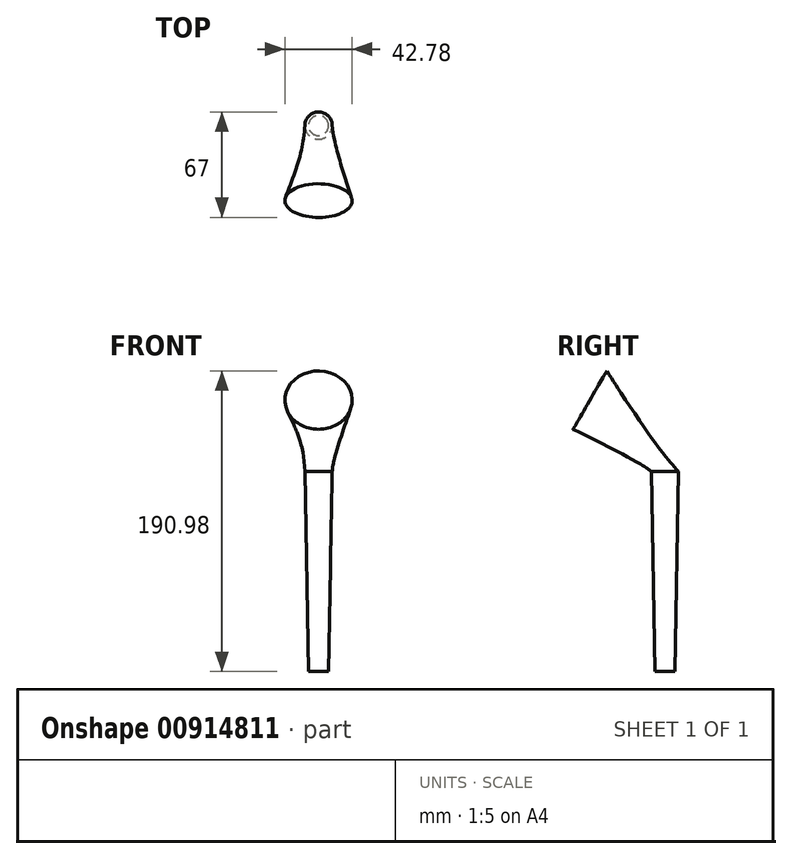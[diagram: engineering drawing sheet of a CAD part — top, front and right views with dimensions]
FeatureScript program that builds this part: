
annotation { "Feature Type Name" : "Feature", "Feature Type Description" : "" }
export const myFeature = defineFeature(function(context is Context, id is Id, definition is map)
    precondition{}
    {
        {
            var Q0;
            Q0=qCreatedBy(makeId("Top.planeOp"),FACE);
            var sketch = newSketch(context, id + "F0", { "sketchPlane" : qUnion([Q0])});
            skCircle(sketch, "E0", {"center": v(0, 0) * mm, "radius": 6.35 * mm});
            skSolve(sketch);
        }
        {
            var Q0;
            Q0=qCreatedBy(makeId("Top.planeOp"),FACE);
            cPlane(context, id + "F1", {"entities" : qUnion([Q0]), "cplaneType" : CPlaneType.OFFSET, "offset" : 127 * mm, "width" : 152.4 * mm, "height" : 152.4 * mm});
        }
        {
            var Q0;
            Q0=qCreatedBy(id+"F1.planeOp",FACE);
            var sketch = newSketch(context, id + "F2", { "sketchPlane" : qUnion([Q0])});
            skCircle(sketch, "E1", {"center": v(0, 0) * mm, "radius": 8.67 * mm});
            skSolve(sketch);
        }
        {
            var Q0;
            Q0=qCreatedBy(id+"F1.planeOp",FACE);
            var sketch = newSketch(context, id + "F3", { "sketchPlane" : qUnion([Q0])});
            skLineSegment(sketch, "E2", {"start": v(-41.24, -0.56) * mm, "end": v(44.89, -0.56) * mm});
            skSolve(sketch);
        }
        {
            var Q0;
            Q0=sQuery(id+"F3.wireOp",EDGE,"E2");
            cPlane(context, id + "F4", {"entities" : qUnion([Q0]), "cplaneType" : CPlaneType.LINE_ANGLE, "offset" : 25.4 * mm, "angle" : 30 * degree, "oppositeDirection" : true, "width" : 152.4 * mm, "height" : 152.4 * mm});
        }
        {
            var Q0;
            Q0=qCreatedBy(id+"F4.planeOp",FACE);
            cPlane(context, id + "F5", {"entities" : qUnion([Q0]), "cplaneType" : CPlaneType.OFFSET, "offset" : 63.5 * mm, "oppositeDirection" : true, "width" : 152.4 * mm, "height" : 152.4 * mm});
        }
        {
            var Q0;
            Q0 = qSketchRegion(id + "F0", true);
            var Q1;
            Q1 = qSketchRegion(id + "F2", true);
            loft(context, id + "F6", {"sheetProfilesArray" : [{ "sheetProfileEntities" : qUnion([Q0]) }, { "sheetProfileEntities" : qUnion([Q1]) }]});
        }
        {
            var Q0;
            Q0=qCreatedBy(id+"F5.planeOp",FACE);
            var sketch = newSketch(context, id + "F7", { "sketchPlane" : qUnion([Q0])});
            skCircle(sketch, "E3", {"center": v(0, 125.53) * mm, "radius": 21.39 * mm});
            skSolve(sketch);
        }
        {
            var Q0;
            Q0 = qSketchRegion(id + "F2", true);
            var Q1;
            Q1=makeQuery(id+"F7.imprint","IMPRINT",FACE,{"disambiguationData":[TD([[makeQuery(id+"F7.imprint","IMPRINT",EDGE,{"derivedFrom":sQuery(id+"F7.wireOp",EDGE,"E3")}),1.0]])]});
            loft(context, id + "F8", {"operationType" : NewBodyOperationType.ADD, "sheetProfilesArray" : [{ "sheetProfileEntities" : qUnion([Q0]) }, { "sheetProfileEntities" : qUnion([Q1]) }]});
        }
    });
